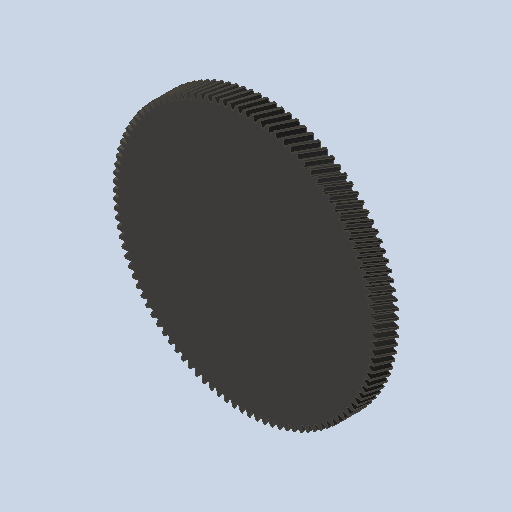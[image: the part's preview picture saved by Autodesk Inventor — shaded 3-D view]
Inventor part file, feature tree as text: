
AUTODESK INVENTOR PART (.ipt)
format: ipt  version: 2023 (Build 270158000, 158)  size: 1,263,104 bytes
history: native  units: mm (DEFAULTED — no unit token found)
features: plane x3, other x3, sketch x2, extrude x1
ambient origin geometry x8: Origin, YZ Plane, XZ Plane, XY Plane, X Axis, Y Axis, Z Axis, Center Point
bodies: Solid1 (feature_tree)
feature tree (9):
  extrude  "Extrusion1"  Depth=15.0mm TaperAngle=0.0deg
  plane  "Work Plane2"
  plane  "Work Plane8"
  plane  "Work Plane9"
  other  "Spur Gear"
  sketch  "Sketch1"  dims[d0=174.274667mm d1=15.0mm d2=0.0mm]
  sketch  "Sketch2"  dims[d3=170.800532mm d4=10.0mm d5=0.0mm d16=101.6mm d17=0.0mm d34=0.293607mm d39=0.0mm d41=0.0mm d43=101.6mm d46=101.6mm d47=0.0mm d48=0.0mm]
  other  "Srf1"
  other  "Pitch Diameter"
